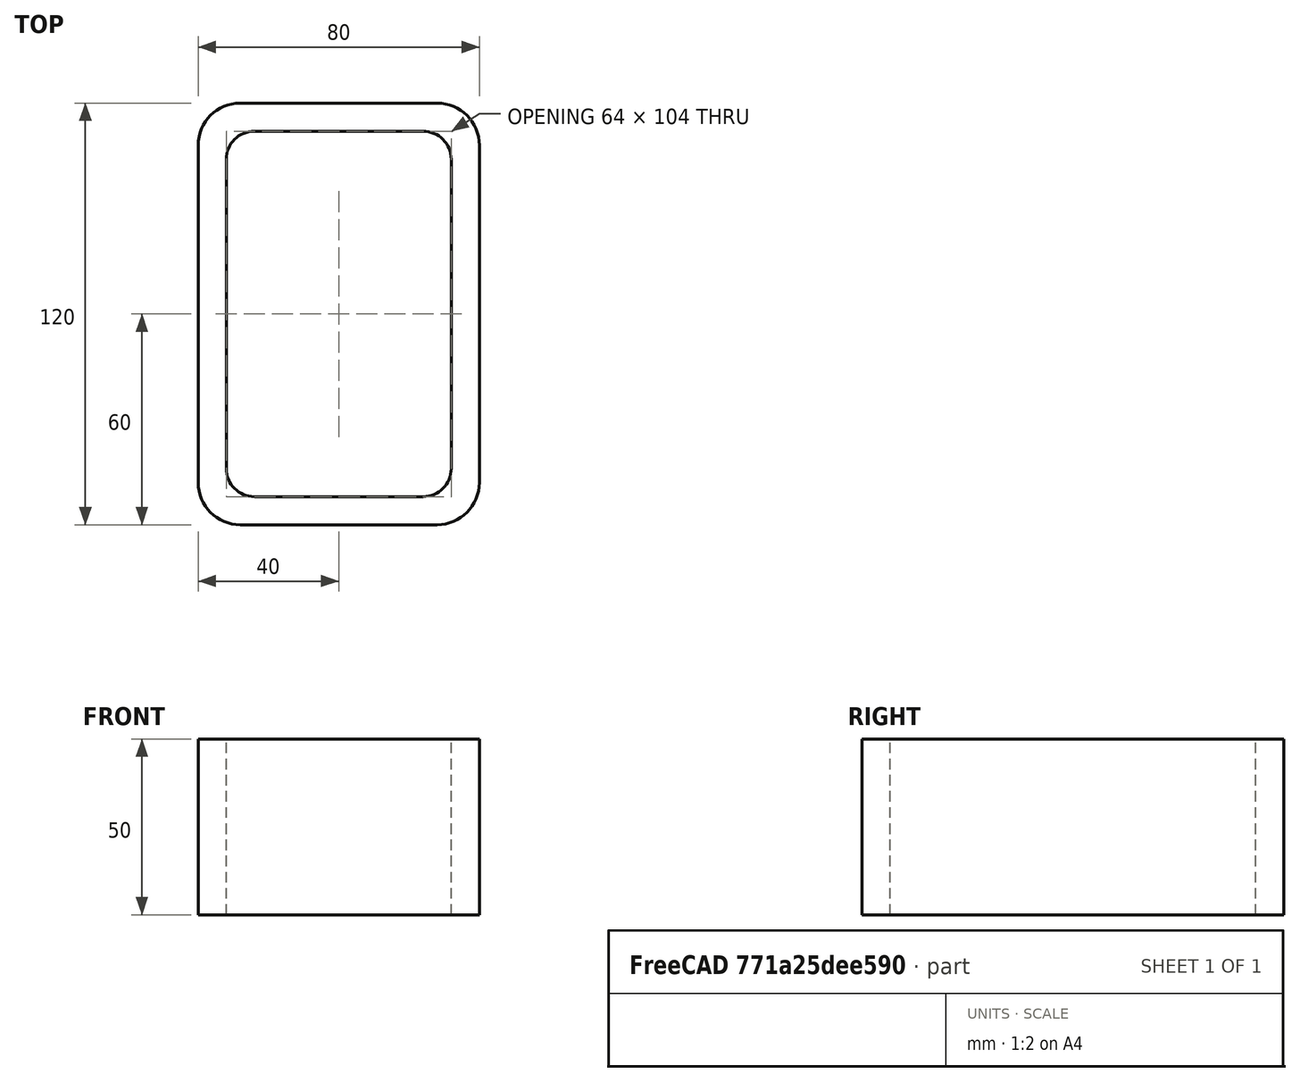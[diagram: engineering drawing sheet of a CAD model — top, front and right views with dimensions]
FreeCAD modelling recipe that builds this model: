
FCSTD DOCUMENT  (FreeCAD 0.15R4671 (Git))
Label: Rectangular hollow section 120x80x8 EN10219 S235JRH
License: All rights reserved
LicenseURL: http://en.wikipedia.org/wiki/All_rights_reserved
objects: Sketcher::SketchObject×1, Part::Extrusion×1
note: 2 computed .brp shape members not serialized (recipe doc carries the construction recipe); baked Part::Feature solids carry a one-line shape summary decoded from their .brp

FEATURE [Sketcher::SketchObject] Sketch
  sketch-geometry (16):
    g0: LineSegment StartX=-24 StartY=52 StartZ=0 EndX=24 EndY=52 EndZ=0
    g1: LineSegment StartX=32 StartY=44 StartZ=0 EndX=32 EndY=-44 EndZ=0
    g2: LineSegment StartX=24 StartY=-52 StartZ=0 EndX=-24 EndY=-52 EndZ=0
    g3: LineSegment StartX=-32 StartY=-44 StartZ=0 EndX=-32 EndY=44 EndZ=0
    g4: LineSegment StartX=-28 StartY=60 StartZ=0 EndX=28 EndY=60 EndZ=0
    g5: LineSegment StartX=40 StartY=48 StartZ=0 EndX=40 EndY=-48 EndZ=0
    g6: LineSegment StartX=28 StartY=-60 StartZ=0 EndX=-28 EndY=-60 EndZ=0
    g7: LineSegment StartX=-40 StartY=-48 StartZ=0 EndX=-40 EndY=48 EndZ=0
    g8: ArcOfCircle CenterX=-24 CenterY=44 CenterZ=0 NormalX=0 NormalY=0 NormalZ=1 Radius=8 StartAngle=1.5708 EndAngle=3.14159
    g9: ArcOfCircle CenterX=24 CenterY=44 CenterZ=0 NormalX=0 NormalY=0 NormalZ=1 Radius=8 StartAngle=0 EndAngle=1.5708
    g10: ArcOfCircle CenterX=24 CenterY=-44 CenterZ=0 NormalX=0 NormalY=0 NormalZ=1 Radius=8 StartAngle=4.71239 EndAngle=6.28319
    g11: ArcOfCircle CenterX=-24 CenterY=-44 CenterZ=0 NormalX=0 NormalY=0 NormalZ=1 Radius=8 StartAngle=3.14159 EndAngle=4.71239
    g12: ArcOfCircle CenterX=28 CenterY=48 CenterZ=0 NormalX=0 NormalY=0 NormalZ=1 Radius=12 StartAngle=0 EndAngle=1.5708
    g13: ArcOfCircle CenterX=28 CenterY=-48 CenterZ=0 NormalX=0 NormalY=0 NormalZ=1 Radius=12 StartAngle=4.71239 EndAngle=6.28319
    g14: ArcOfCircle CenterX=-28 CenterY=-48 CenterZ=0 NormalX=0 NormalY=0 NormalZ=1 Radius=12 StartAngle=3.14159 EndAngle=4.71239
    g15: ArcOfCircle CenterX=-28 CenterY=48 CenterZ=0 NormalX=0 NormalY=0 NormalZ=1 Radius=12 StartAngle=1.5708 EndAngle=3.14159
  constraints (36):
    c: Horizontal(g2)
    c: Vertical(g3)
    c: Horizontal(g6)
    c: Vertical(g7)
    c: Tangent(g3,g8) = 1.5708
    c: Tangent(g0,g8) = 1.5708
    c: Tangent(g0,g9) = 1.5708
    c: Tangent(g1,g9) = 1.5708
    c: Tangent(g1,g10) = 1.5708
    c: Tangent(g2,g10) = 1.5708
    c: Tangent(g2,g11) = 1.5708
    c: Tangent(g3,g11) = 1.5708
    c: Tangent(g4,g12) = 1.5708
    c: Tangent(g5,g12) = 1.5708
    c: Tangent(g5,g13) = 1.5708
    c: Tangent(g6,g13) = 1.5708
    c: Tangent(g6,g14) = 1.5708
    c: Tangent(g7,g14) = 1.5708
    c: Tangent(g7,g15) = 1.5708
    c: Tangent(g4,g15) = 1.5708
    c: Equal(g9,g8)
    c: Equal(g9,g11)
    c: Equal(g9,g10)
    c: Equal(g12,g15)
    c: Equal(g12,g14)
    c: Equal(g12,g13)
    c: Symmetric(g4,g6,g-1)
    c: Symmetric(g7,g5,g-2)
    c: DistanceY(g4,g6) = -120
    c: DistanceX(g7,g5) = 80
    c: Symmetric(g3,g1,g-2)
    c: Symmetric(g0,g2,g-1)
    c: DistanceY(g0,g4) = 8
    c: DistanceX(g5,g1) = -8
    c: Radius(g9) = 8
    c: Radius(g12) = 12
FEATURE [Part::Extrusion] Extrude  label="Rectangular hollow section 120x80x8 EN10219 S235JRH"
  Base = -> Sketch
  Dir = (0,0,50)
  Solid = true
